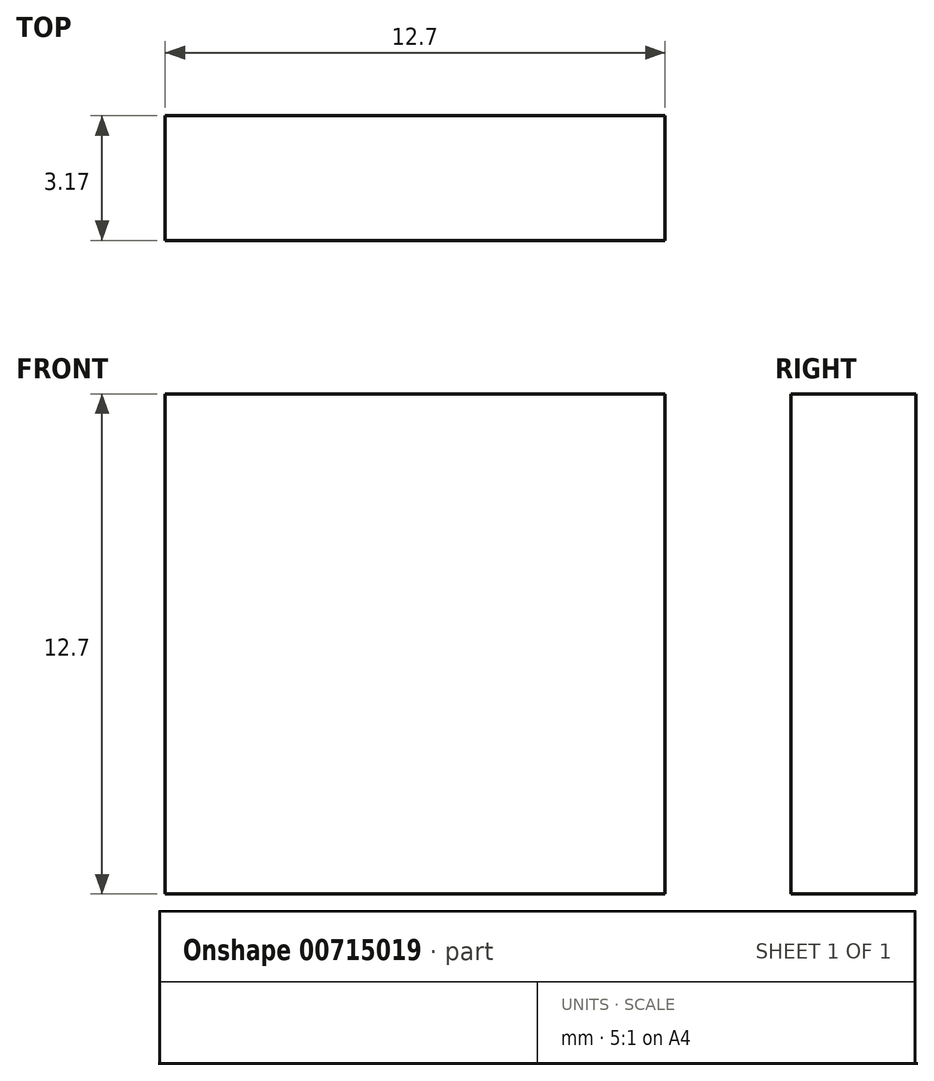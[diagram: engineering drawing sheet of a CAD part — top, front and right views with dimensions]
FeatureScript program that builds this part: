
annotation { "Feature Type Name" : "Feature", "Feature Type Description" : "" }
export const myFeature = defineFeature(function(context is Context, id is Id, definition is map)
    precondition{}
    {
        {
            var Q0;
            Q0=qCreatedBy(makeId("Front.planeOp"),FACE);
            var sketch = newSketch(context, id + "F0", { "sketchPlane" : qUnion([Q0])});
            skLineSegment(sketch, "E0.bottom", {"start": v(-6.35, 6.35) * mm, "end": v(6.35, 6.35) * mm});
            skLineSegment(sketch, "E0.top", {"start": v(-6.35, -6.35) * mm, "end": v(6.35, -6.35) * mm});
            skLineSegment(sketch, "E0.left", {"start": v(-6.35, 6.35) * mm, "end": v(-6.35, -6.35) * mm});
            skLineSegment(sketch, "E0.right", {"start": v(6.35, 6.35) * mm, "end": v(6.35, -6.35) * mm});
            skPoint(sketch, "E0.middle", {"position": v(0, 0) * mm});
            skSolve(sketch);
        }
        {
            var Q0;
            Q0 = qSketchRegion(id + "F0", true);
            var Q1;
            Q1=makeQuery(id+"F0.imprint","IMPRINT",FACE,{"disambiguationData":[TD([[makeQuery(id+"F0.imprint","IMPRINT",EDGE,{"derivedFrom":sQuery(id+"F0.wireOp",EDGE,"E0.bottom")}),-1.0]])]});
            extrude(context, id + "F1", {"entities" : qUnion([Q0, Q1]), "depth" : 3.17 * mm, "offsetDistance" : 25.4 * mm});
        }
    });
